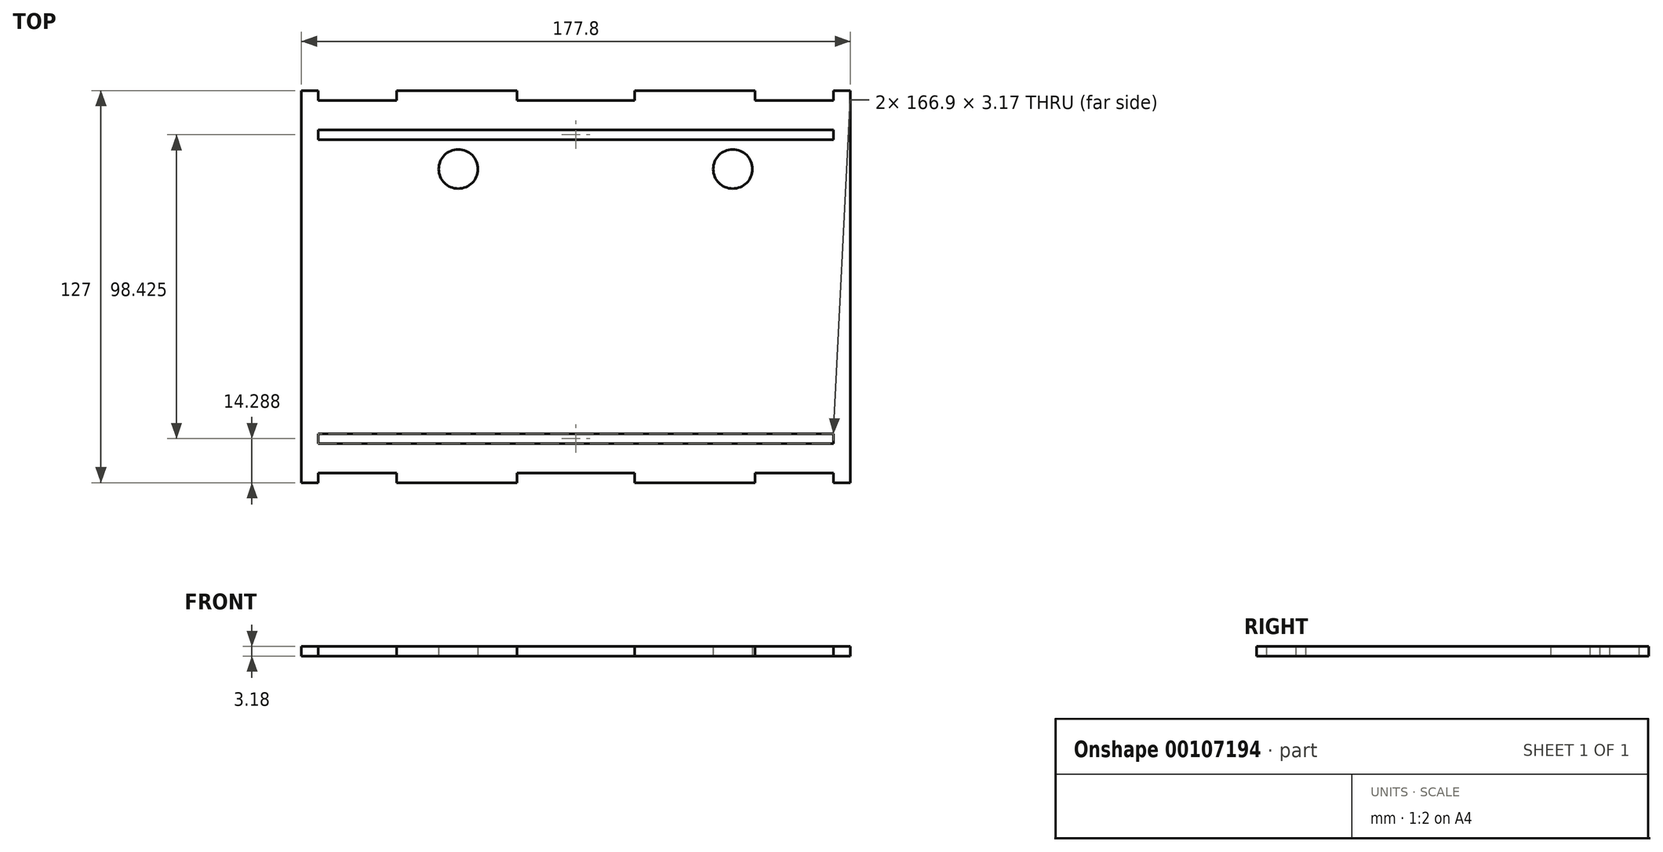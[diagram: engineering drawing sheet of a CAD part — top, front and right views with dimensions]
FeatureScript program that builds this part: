
annotation { "Feature Type Name" : "Feature", "Feature Type Description" : "" }
export const myFeature = defineFeature(function(context is Context, id is Id, definition is map)
    precondition{}
    {
        {
            var Q0;
            Q0=qCreatedBy(makeId("Top.planeOp"),FACE);
            var sketch = newSketch(context, id + "F0", { "sketchPlane" : qUnion([Q0])});
            skCircle(sketch, "E0", {"center": v(63.5, 38.1) * mm, "radius": 6.35 * mm});
            skCircle(sketch, "E1", {"center": v(-25.4, 38.1) * mm, "radius": 6.35 * mm});
            skLineSegment(sketch, "E2", {"start": v(-76.2, 63.5) * mm, "end": v(-76.2, -63.5) * mm});
            skLineSegment(sketch, "E3.bottom", {"start": v(-76.2, 63.5) * mm, "end": v(-70.75, 63.5) * mm});
            skLineSegment(sketch, "E3.right", {"start": v(101.6, 63.5) * mm, "end": v(101.6, -63.5) * mm});
            skCircle(sketch, "E4.MirrorC", {"center": v(63.5, -38.1) * mm, "radius": 6.35 * mm});
            skCircle(sketch, "E5.MirrorC", {"center": v(-25.4, -38.1) * mm, "radius": 6.35 * mm});
            skPoint(sketch, "E6", {"position": v(12.7, 76.2) * mm});
            skPoint(sketch, "E7", {"position": v(12.7, 63.5) * mm});
            skLineSegment(sketch, "E8.MirrorCS", {"start": v(70.75, 63.5) * mm, "end": v(70.75, 60.32) * mm});
            skLineSegment(sketch, "E9.MirrorCS", {"start": v(31.75, 60.32) * mm, "end": v(-6.35, 60.32) * mm});
            skLineSegment(sketch, "E10.MirrorCS", {"start": v(-70.75, 60.32) * mm, "end": v(-45.35, 60.32) * mm});
            skLineSegment(sketch, "E11.MirrorCS", {"start": v(-6.35, 63.5) * mm, "end": v(-6.35, 60.32) * mm});
            skLineSegment(sketch, "E12.MirrorCS", {"start": v(-70.75, 63.5) * mm, "end": v(-70.75, 60.32) * mm});
            skLineSegment(sketch, "E13.MirrorCS", {"start": v(96.15, 63.5) * mm, "end": v(96.15, 60.32) * mm});
            skLineSegment(sketch, "E14.MirrorCS", {"start": v(96.15, 60.32) * mm, "end": v(70.75, 60.32) * mm});
            skLineSegment(sketch, "E15.MirrorCS", {"start": v(31.75, 63.5) * mm, "end": v(31.75, 60.32) * mm});
            skLineSegment(sketch, "E16.MirrorCS", {"start": v(-45.35, 63.5) * mm, "end": v(-45.35, 60.32) * mm});
            skLineSegment(sketch, "E17.trimOffspring", {"start": v(-45.35, 63.5) * mm, "end": v(-6.35, 63.5) * mm});
            skLineSegment(sketch, "E18.trimOffspring", {"start": v(31.75, 63.5) * mm, "end": v(70.75, 63.5) * mm});
            skLineSegment(sketch, "E19.trimOffspring", {"start": v(96.15, 63.5) * mm, "end": v(101.6, 63.5) * mm});
            skLineSegment(sketch, "E20.MirrorCS", {"start": v(96.15, 47.63) * mm, "end": v(96.15, 50.8) * mm});
            skLineSegment(sketch, "E21.MirrorCS", {"start": v(-70.75, 47.63) * mm, "end": v(-70.75, 50.8) * mm});
            skLineSegment(sketch, "E22.MirrorCS", {"start": v(-70.75, 50.8) * mm, "end": v(-45.35, 50.8) * mm});
            skLineSegment(sketch, "E23.MirrorCS", {"start": v(31.75, 50.8) * mm, "end": v(-6.35, 50.8) * mm});
            skLineSegment(sketch, "E24.MirrorCS", {"start": v(96.15, 47.63) * mm, "end": v(70.75, 47.63) * mm});
            skLineSegment(sketch, "E25.MirrorCS", {"start": v(-45.35, 47.63) * mm, "end": v(-70.75, 47.63) * mm});
            skLineSegment(sketch, "E26.MirrorCS", {"start": v(96.15, 50.8) * mm, "end": v(70.75, 50.8) * mm});
            skLineSegment(sketch, "E27.MirrorCS", {"start": v(31.75, 47.63) * mm, "end": v(-6.35, 47.63) * mm});
            skPoint(sketch, "E28.MirrorP", {"position": v(12.7, 50.8) * mm});
            skLineSegment(sketch, "E29.MirrorCS", {"start": v(-70.75, -63.5) * mm, "end": v(-70.75, -60.32) * mm});
            skLineSegment(sketch, "E30.MirrorCS", {"start": v(-76.2, -63.5) * mm, "end": v(-70.75, -63.5) * mm});
            skLineSegment(sketch, "E31.MirrorCS", {"start": v(-6.35, -63.5) * mm, "end": v(-6.35, -60.32) * mm});
            skLineSegment(sketch, "E32.MirrorCS", {"start": v(96.15, -63.5) * mm, "end": v(96.15, -60.32) * mm});
            skLineSegment(sketch, "E33.MirrorCS", {"start": v(31.75, -63.5) * mm, "end": v(31.75, -60.32) * mm});
            skLineSegment(sketch, "E34.MirrorCS", {"start": v(70.75, -63.5) * mm, "end": v(70.75, -60.32) * mm});
            skLineSegment(sketch, "E35.MirrorCS", {"start": v(96.15, -63.5) * mm, "end": v(101.6, -63.5) * mm});
            skLineSegment(sketch, "E36.MirrorCS", {"start": v(-45.35, -63.5) * mm, "end": v(-45.35, -60.32) * mm});
            skPoint(sketch, "E37.MirrorP", {"position": v(12.7, -76.2) * mm});
            skLineSegment(sketch, "E38.MirrorCS", {"start": v(31.75, -63.5) * mm, "end": v(70.75, -63.5) * mm});
            skPoint(sketch, "E39.MirrorP", {"position": v(12.7, -63.5) * mm});
            skLineSegment(sketch, "E40.MirrorCS", {"start": v(-45.35, -63.5) * mm, "end": v(-6.35, -63.5) * mm});
            skLineSegment(sketch, "E41.MirrorCS", {"start": v(-70.75, -60.32) * mm, "end": v(-45.35, -60.32) * mm});
            skLineSegment(sketch, "E42.MirrorCS", {"start": v(96.15, -60.32) * mm, "end": v(70.75, -60.32) * mm});
            skLineSegment(sketch, "E43.MirrorCS", {"start": v(31.75, -60.32) * mm, "end": v(-6.35, -60.32) * mm});
            skLineSegment(sketch, "E44.MirrorCS", {"start": v(-70.75, -47.63) * mm, "end": v(-70.75, -50.8) * mm});
            skLineSegment(sketch, "E45.MirrorCS", {"start": v(96.15, -47.63) * mm, "end": v(96.15, -50.8) * mm});
            skLineSegment(sketch, "E46.MirrorCS", {"start": v(-70.75, -50.8) * mm, "end": v(-45.35, -50.8) * mm});
            skPoint(sketch, "E47.MirrorP", {"position": v(12.7, -50.8) * mm});
            skLineSegment(sketch, "E48.MirrorCS", {"start": v(31.75, -47.63) * mm, "end": v(-6.35, -47.63) * mm});
            skLineSegment(sketch, "E49.MirrorCS", {"start": v(31.75, -50.8) * mm, "end": v(-6.35, -50.8) * mm});
            skLineSegment(sketch, "E50.MirrorCS", {"start": v(96.15, -47.63) * mm, "end": v(70.75, -47.63) * mm});
            skLineSegment(sketch, "E51.MirrorCS", {"start": v(-45.35, -47.63) * mm, "end": v(-70.75, -47.63) * mm});
            skLineSegment(sketch, "E52.MirrorCS", {"start": v(96.15, -50.8) * mm, "end": v(70.75, -50.8) * mm});
            skLineSegment(sketch, "E53", {"start": v(-45.35, 50.8) * mm, "end": v(70.75, 50.8) * mm});
            skLineSegment(sketch, "E54", {"start": v(70.75, 47.63) * mm, "end": v(-45.35, 47.63) * mm});
            skLineSegment(sketch, "E55", {"start": v(-45.35, -47.63) * mm, "end": v(70.75, -47.63) * mm});
            skLineSegment(sketch, "E56", {"start": v(70.75, -50.8) * mm, "end": v(-45.35, -50.8) * mm});
            skSolve(sketch);
        }
        {
            var Q0;
            Q0=makeQuery(id+"F0.imprint","IMPRINT",FACE,{"disambiguationData":[TD([[makeQuery(id+"F0.imprint","IMPRINT",EDGE,{"derivedFrom":sQuery(id+"F0.wireOp",EDGE,"921fbad8-19a0-49b5-be16-62b8bbc91783")}),-1.0]])]});
            var Q1;
            Q1=makeQuery(id+"F0.imprint","IMPRINT",FACE,{"disambiguationData":[TD([[makeQuery(id+"F0.imprint","IMPRINT",EDGE,{"derivedFrom":sQuery(id+"F0.wireOp",EDGE,"E0")}),-1.0]])]});
            var Q2;
            Q2=makeQuery(id+"F0.imprint","IMPRINT",FACE,{"disambiguationData":[TD([[makeQuery(id+"F0.imprint","IMPRINT",EDGE,{"derivedFrom":sQuery(id+"F0.wireOp",EDGE,"E1")}),-1.0]])]});
            var Q3;
            Q3=makeQuery(id+"F0.imprint","IMPRINT",FACE,{"disambiguationData":[TD([[makeQuery(id+"F0.imprint","IMPRINT",EDGE,{"derivedFrom":sQuery(id+"F0.wireOp",EDGE,"E5.MirrorC")}),1.0]])]});
            var Q4;
            Q4=makeQuery(id+"F0.imprint","IMPRINT",FACE,{"disambiguationData":[TD([[makeQuery(id+"F0.imprint","IMPRINT",EDGE,{"derivedFrom":sQuery(id+"F0.wireOp",EDGE,"E4.MirrorC")}),1.0]])]});
            extrude(context, id + "F1", {"entities" : qUnion([Q0, Q1, Q2, Q3, Q4]), "depth" : 3.17 * mm});
        }
    });
